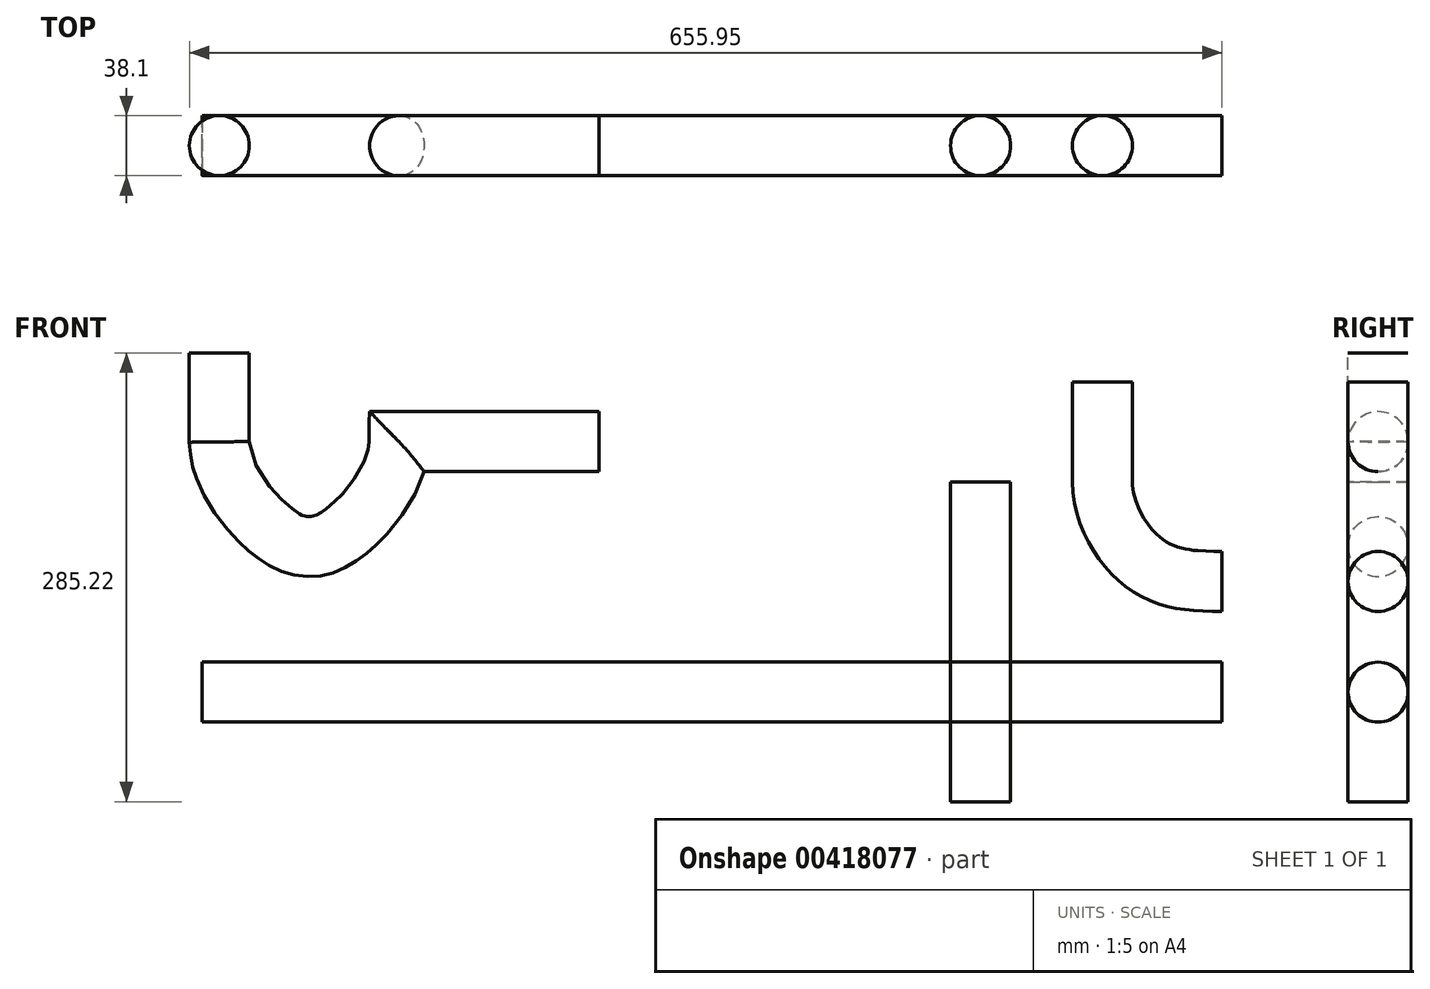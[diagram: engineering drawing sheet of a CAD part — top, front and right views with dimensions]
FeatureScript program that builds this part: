
annotation { "Feature Type Name" : "Feature", "Feature Type Description" : "" }
export const myFeature = defineFeature(function(context is Context, id is Id, definition is map)
    precondition{}
    {
        {
            var Q0;
            Q0=qCreatedBy(makeId("Front.planeOp"),FACE);
            var sketch = newSketch(context, id + "F0", { "sketchPlane" : qUnion([Q0])});
            skLineSegment(sketch, "E0", {"start": v(0, 0) * mm, "end": v(0, 63.5) * mm});
            skFitSpline(sketch, "E1", {"points": [v(0, 0) * mm, v(25.4, -50.8) * mm, v(76.2, -63.5) * mm], "startDerivative": vector(0, -115.23) * mm, "endDerivative": vector(136.83, 0) * mm});
            skLineSegment(sketch, "E2", {"start": v(76.2, -133.9) * mm, "end": v(-571.5, -133.9) * mm});
            skLineSegment(sketch, "E3", {"start": v(-76.5, 0) * mm, "end": v(-76.5, -203.2) * mm});
            skLineSegment(sketch, "E4", {"start": v(-560.84, 82.02) * mm, "end": v(-560.84, 25.4) * mm});
            skLineSegment(sketch, "E5", {"start": v(-446.54, 25.4) * mm, "end": v(-319.54, 25.4) * mm});
            skFitSpline(sketch, "E6", {"points": [v(-560.84, 25.4) * mm, v(-522.74, -34.82) * mm, v(-503.7, -41.17) * mm, v(-484.64, -34.82) * mm, v(-446.54, 25.4) * mm], "startDerivative": vector(5.53, -233.3) * mm, "endDerivative": vector(5.42, 233.3) * mm});
            skSolve(sketch);
        }
        {
            var Q0;
            Q0=sQuery(id+"F0.wireOp",VERTEX,"E1.2.internal");
            var Q1;
            Q1=sQuery(id+"F0.wireOp",EDGE,"E1");
            cPlane(context, id + "F1", {"entities" : qUnion([Q0, Q1]), "cplaneType" : CPlaneType.CURVE_POINT, "offset" : 25.4 * mm, "width" : 152.4 * mm, "height" : 152.4 * mm});
        }
        {
            var Q0;
            Q0=qCreatedBy(id+"F1.planeOp",FACE);
            var sketch = newSketch(context, id + "F2", { "sketchPlane" : qUnion([Q0])});
            skCircle(sketch, "E7", {"center": v(0, -63.28) * mm, "radius": 19.05 * mm});
            skCircle(sketch, "E8", {"center": v(0, -133.53) * mm, "radius": 19.05 * mm});
            skSolve(sketch);
        }
        {
            var Q0;
            Q0=makeQuery(id+"F2.imprint","IMPRINT",FACE,{"disambiguationData":[TD([[makeQuery(id+"F2.imprint","IMPRINT",EDGE,{"derivedFrom":sQuery(id+"F2.wireOp",EDGE,"E7")}),1.0]])]});
            var Q1;
            Q1=sQuery(id+"F0.wireOp",EDGE,"E1");
            var Q2;
            Q2=sQuery(id+"F0.wireOp",EDGE,"E0");
            sweep(context, id + "F3", {"profiles" : qUnion([Q0]), "path" : qUnion([Q1, Q2])});
        }
        {
            var Q0;
            Q0=makeQuery(id+"F2.imprint","IMPRINT",FACE,{"disambiguationData":[TD([[makeQuery(id+"F2.imprint","IMPRINT",EDGE,{"derivedFrom":sQuery(id+"F2.wireOp",EDGE,"E8")}),1.0]])]});
            var Q1;
            Q1=sQuery(id+"F0.wireOp",EDGE,"E2");
            sweep(context, id + "F4", {"profiles" : qUnion([Q0]), "path" : qUnion([Q1])});
        }
        {
            var Q0;
            Q0=qCreatedBy(makeId("Top.planeOp"),FACE);
            var sketch = newSketch(context, id + "F5", { "sketchPlane" : qUnion([Q0])});
            skCircle(sketch, "E9", {"center": v(-77.22, 0) * mm, "radius": 19.05 * mm});
            skSolve(sketch);
        }
        {
            var Q0;
            Q0=makeQuery(id+"F5.imprint","IMPRINT",FACE,{"disambiguationData":[TD([[makeQuery(id+"F5.imprint","IMPRINT",EDGE,{"derivedFrom":sQuery(id+"F5.wireOp",EDGE,"E9")}),1.0]])]});
            var Q1;
            Q1=sQuery(id+"F0.wireOp",EDGE,"E3");
            sweep(context, id + "F6", {"profiles" : qUnion([Q0]), "path" : qUnion([Q1])});
        }
        {
            var Q0;
            Q0=sQuery(id+"F0.wireOp",EDGE,"E5");
            var Q1;
            Q1=sQuery(id+"F0.wireOp",VERTEX,"E5.end");
            cPlane(context, id + "F7", {"entities" : qUnion([Q0, Q1]), "cplaneType" : CPlaneType.LINE_POINT, "offset" : 25.4 * mm, "width" : 152.4 * mm, "height" : 152.4 * mm});
        }
        {
            var Q0;
            Q0=qCreatedBy(id+"F7.planeOp",FACE);
            var sketch = newSketch(context, id + "F8", { "sketchPlane" : qUnion([Q0])});
            skCircle(sketch, "E10", {"center": v(0, 25.54) * mm, "radius": 19.05 * mm});
            skSolve(sketch);
        }
        {
            var Q0;
            Q0=makeQuery(id+"F8.imprint","IMPRINT",FACE,{"disambiguationData":[TD([[makeQuery(id+"F8.imprint","IMPRINT",EDGE,{"derivedFrom":sQuery(id+"F8.wireOp",EDGE,"E10")}),1.0]])]});
            var Q1;
            Q1=sQuery(id+"F0.wireOp",EDGE,"E5");
            var Q2;
            Q2=sQuery(id+"F0.wireOp",EDGE,"E6");
            var Q3;
            Q3=sQuery(id+"F0.wireOp",EDGE,"E4");
            sweep(context, id + "F9", {"profiles" : qUnion([Q0]), "path" : qUnion([Q1, Q2, Q3])});
        }
    });
